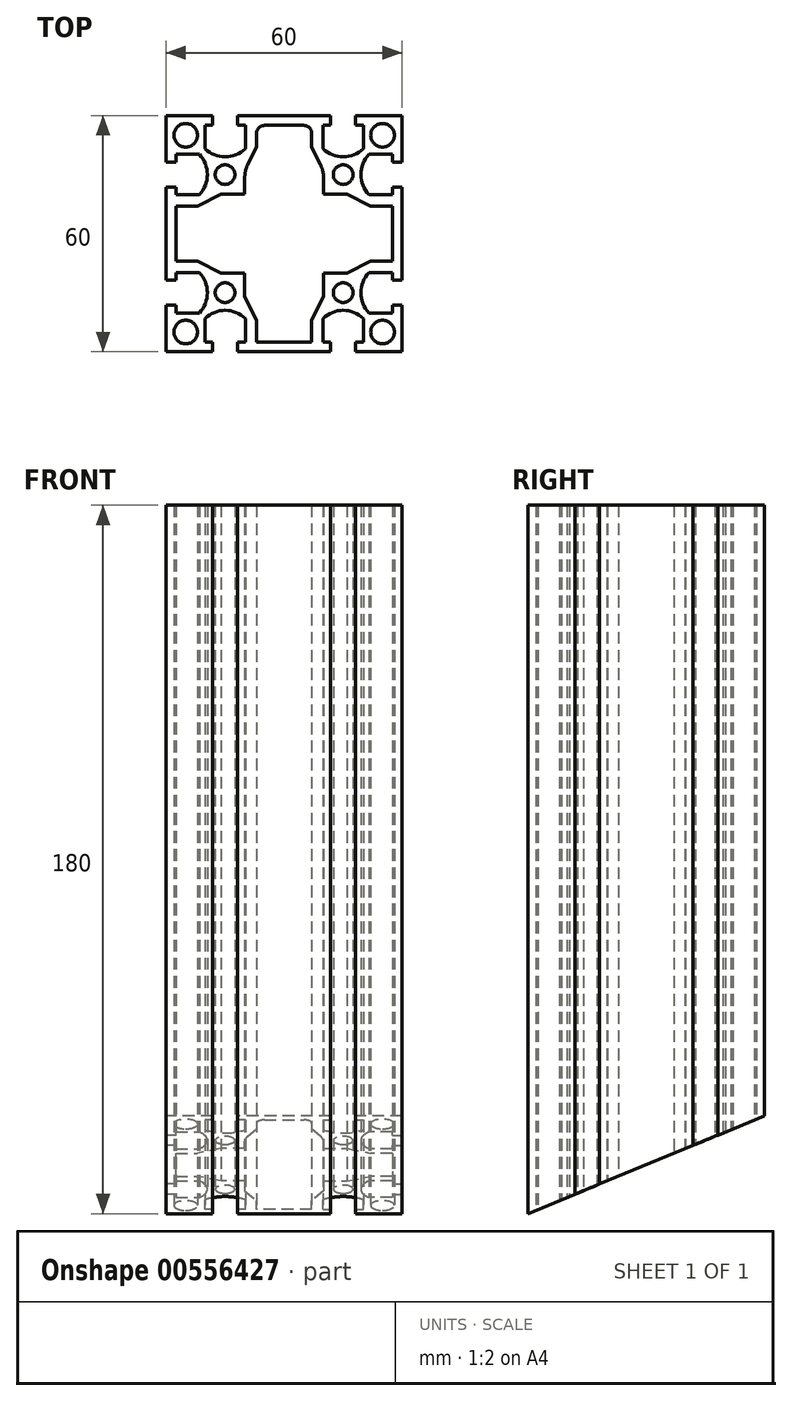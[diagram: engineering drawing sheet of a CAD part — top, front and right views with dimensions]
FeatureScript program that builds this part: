
annotation { "Feature Type Name" : "Feature", "Feature Type Description" : "" }
export const myFeature = defineFeature(function(context is Context, id is Id, definition is map)
    precondition{}
    {
        {
            var Q0;
            Q0=qCreatedBy(makeId("Top.planeOp"),FACE);
            var sketch = newSketch(context, id + "F0", { "sketchPlane" : qUnion([Q0])});
            skLineSegment(sketch, "E0.bottom", {"start": v(30, -30) * mm, "end": v(-30, -30) * mm});
            skLineSegment(sketch, "E0.top", {"start": v(30, 30) * mm, "end": v(-30, 30) * mm});
            skLineSegment(sketch, "E0.left", {"start": v(30, -30) * mm, "end": v(30, 30) * mm});
            skLineSegment(sketch, "E0.right", {"start": v(-30, -30) * mm, "end": v(-30, 30) * mm});
            skPoint(sketch, "E0.middle", {"position": v(0, 0) * mm});
            skLineSegment(sketch, "E1.top", {"start": v(-11.85, 30) * mm, "end": v(-18.15, 30) * mm});
            skLineSegment(sketch, "E1.left", {"start": v(-11.85, 27.5) * mm, "end": v(-11.85, 30) * mm});
            skLineSegment(sketch, "E1.right", {"start": v(-18.15, 27.5) * mm, "end": v(-18.15, 30) * mm});
            skPoint(sketch, "E1.middle", {"position": v(-15, 28.75) * mm});
            skLineSegment(sketch, "E2.bottom", {"start": v(-9.85, 27.5) * mm, "end": v(-11.85, 27.5) * mm});
            skLineSegment(sketch, "E2.left", {"start": v(-9.85, 27.5) * mm, "end": v(-9.85, 21.55) * mm});
            skLineSegment(sketch, "E2.right", {"start": v(-20.15, 27.5) * mm, "end": v(-20.15, 21.55) * mm});
            skPoint(sketch, "E2.middle", {"position": v(-15, 24.52) * mm});
            skArc(sketch, "E3", {"start": v(-20.15, 21.55) * mm, "mid": v(-15, 19.5) * mm, "end": v(-9.85, 21.55) * mm});
            skPoint(sketch, "E4.MirrorP", {"position": v(15, 24.52) * mm});
            skPoint(sketch, "E5.MirrorP", {"position": v(15, 28.75) * mm});
            skLineSegment(sketch, "E6.MirrorCS", {"start": v(11.85, 27.5) * mm, "end": v(11.85, 30) * mm});
            skLineSegment(sketch, "E7.MirrorCS", {"start": v(18.15, 27.5) * mm, "end": v(18.15, 30) * mm});
            skLineSegment(sketch, "E8.MirrorCS", {"start": v(9.85, 27.5) * mm, "end": v(11.85, 27.5) * mm});
            skLineSegment(sketch, "E9.MirrorCS", {"start": v(9.85, 27.5) * mm, "end": v(9.85, 21.55) * mm});
            skArc(sketch, "E10.MirrorCS", {"start": v(20.15, 21.55) * mm, "mid": v(15, 19.5) * mm, "end": v(9.85, 21.55) * mm});
            skLineSegment(sketch, "E11.MirrorCS", {"start": v(20.15, 27.5) * mm, "end": v(20.15, 21.55) * mm});
            skLineSegment(sketch, "E12.MirrorCS", {"start": v(11.85, 30) * mm, "end": v(18.15, 30) * mm});
            skLineSegment(sketch, "E13.1.0", {"start": v(27.5, 20.15) * mm, "end": v(21.55, 20.15) * mm});
            skLineSegment(sketch, "E13.1.1", {"start": v(27.5, 9.85) * mm, "end": v(21.55, 9.85) * mm});
            skArc(sketch, "E13.1.2", {"start": v(21.55, 20.15) * mm, "mid": v(19.5, 15) * mm, "end": v(21.55, 9.85) * mm});
            skLineSegment(sketch, "E13.1.3", {"start": v(27.5, -9.85) * mm, "end": v(21.55, -9.85) * mm});
            skLineSegment(sketch, "E13.1.4", {"start": v(27.5, -20.15) * mm, "end": v(21.55, -20.15) * mm});
            skPoint(sketch, "E13.1.5", {"position": v(28.75, 15) * mm});
            skPoint(sketch, "E13.1.6", {"position": v(28.75, -15) * mm});
            skArc(sketch, "E13.1.7", {"start": v(21.55, -20.15) * mm, "mid": v(19.5, -15) * mm, "end": v(21.55, -9.85) * mm});
            skPoint(sketch, "E13.1.8", {"position": v(24.52, -15) * mm});
            skPoint(sketch, "E13.1.9", {"position": v(24.52, 15) * mm});
            skLineSegment(sketch, "E13.1.10", {"start": v(27.5, 9.85) * mm, "end": v(27.5, 20.15) * mm});
            skLineSegment(sketch, "E13.1.11", {"start": v(27.5, -11.85) * mm, "end": v(27.5, -18.15) * mm});
            skLineSegment(sketch, "E13.1.12", {"start": v(30, 11.85) * mm, "end": v(30, 18.15) * mm});
            skLineSegment(sketch, "E13.1.13", {"start": v(30, -11.85) * mm, "end": v(30, -18.15) * mm});
            skLineSegment(sketch, "E13.1.14", {"start": v(27.5, 18.15) * mm, "end": v(30, 18.15) * mm});
            skLineSegment(sketch, "E13.1.15", {"start": v(27.5, 11.85) * mm, "end": v(30, 11.85) * mm});
            skLineSegment(sketch, "E13.1.16", {"start": v(27.5, 11.85) * mm, "end": v(27.5, 18.15) * mm});
            skLineSegment(sketch, "E13.1.17", {"start": v(27.5, -9.85) * mm, "end": v(27.5, -20.15) * mm});
            skLineSegment(sketch, "E13.1.18", {"start": v(27.5, -18.15) * mm, "end": v(30, -18.15) * mm});
            skLineSegment(sketch, "E13.1.19", {"start": v(27.5, -11.85) * mm, "end": v(30, -11.85) * mm});
            skLineSegment(sketch, "E13.2.0", {"start": v(20.15, -27.5) * mm, "end": v(20.15, -21.55) * mm});
            skLineSegment(sketch, "E13.2.1", {"start": v(9.85, -27.5) * mm, "end": v(9.85, -21.55) * mm});
            skArc(sketch, "E13.2.2", {"start": v(20.15, -21.55) * mm, "mid": v(15, -19.5) * mm, "end": v(9.85, -21.55) * mm});
            skLineSegment(sketch, "E13.2.3", {"start": v(-9.85, -27.5) * mm, "end": v(-9.85, -21.55) * mm});
            skLineSegment(sketch, "E13.2.4", {"start": v(-20.15, -27.5) * mm, "end": v(-20.15, -21.55) * mm});
            skPoint(sketch, "E13.2.5", {"position": v(15, -28.75) * mm});
            skPoint(sketch, "E13.2.6", {"position": v(-15, -28.75) * mm});
            skArc(sketch, "E13.2.7", {"start": v(-20.15, -21.55) * mm, "mid": v(-15, -19.5) * mm, "end": v(-9.85, -21.55) * mm});
            skPoint(sketch, "E13.2.8", {"position": v(-15, -24.52) * mm});
            skPoint(sketch, "E13.2.9", {"position": v(15, -24.52) * mm});
            skLineSegment(sketch, "E13.2.10", {"start": v(9.85, -27.5) * mm, "end": v(20.15, -27.5) * mm});
            skLineSegment(sketch, "E13.2.11", {"start": v(-11.85, -27.5) * mm, "end": v(-18.15, -27.5) * mm});
            skLineSegment(sketch, "E13.2.12", {"start": v(11.85, -30) * mm, "end": v(18.15, -30) * mm});
            skLineSegment(sketch, "E13.2.13", {"start": v(-11.85, -30) * mm, "end": v(-18.15, -30) * mm});
            skLineSegment(sketch, "E13.2.14", {"start": v(18.15, -27.5) * mm, "end": v(18.15, -30) * mm});
            skLineSegment(sketch, "E13.2.15", {"start": v(11.85, -27.5) * mm, "end": v(11.85, -30) * mm});
            skLineSegment(sketch, "E13.2.16", {"start": v(11.85, -27.5) * mm, "end": v(18.15, -27.5) * mm});
            skLineSegment(sketch, "E13.2.17", {"start": v(-9.85, -27.5) * mm, "end": v(-20.15, -27.5) * mm});
            skLineSegment(sketch, "E13.2.18", {"start": v(-18.15, -27.5) * mm, "end": v(-18.15, -30) * mm});
            skLineSegment(sketch, "E13.2.19", {"start": v(-11.85, -27.5) * mm, "end": v(-11.85, -30) * mm});
            skLineSegment(sketch, "E13.3.0", {"start": v(-27.5, -20.15) * mm, "end": v(-21.55, -20.15) * mm});
            skLineSegment(sketch, "E13.3.1", {"start": v(-27.5, -9.85) * mm, "end": v(-21.55, -9.85) * mm});
            skArc(sketch, "E13.3.2", {"start": v(-21.55, -20.15) * mm, "mid": v(-19.5, -15) * mm, "end": v(-21.55, -9.85) * mm});
            skLineSegment(sketch, "E13.3.3", {"start": v(-27.5, 9.85) * mm, "end": v(-21.55, 9.85) * mm});
            skLineSegment(sketch, "E13.3.4", {"start": v(-27.5, 20.15) * mm, "end": v(-21.55, 20.15) * mm});
            skPoint(sketch, "E13.3.5", {"position": v(-28.75, -15) * mm});
            skPoint(sketch, "E13.3.6", {"position": v(-28.75, 15) * mm});
            skArc(sketch, "E13.3.7", {"start": v(-21.55, 20.15) * mm, "mid": v(-19.5, 15) * mm, "end": v(-21.55, 9.85) * mm});
            skPoint(sketch, "E13.3.8", {"position": v(-24.52, 15) * mm});
            skPoint(sketch, "E13.3.9", {"position": v(-24.52, -15) * mm});
            skLineSegment(sketch, "E13.3.10", {"start": v(-27.5, -9.85) * mm, "end": v(-27.5, -20.15) * mm});
            skLineSegment(sketch, "E13.3.11", {"start": v(-27.5, 11.85) * mm, "end": v(-27.5, 18.15) * mm});
            skLineSegment(sketch, "E13.3.12", {"start": v(-30, -11.85) * mm, "end": v(-30, -18.15) * mm});
            skLineSegment(sketch, "E13.3.13", {"start": v(-30, 11.85) * mm, "end": v(-30, 18.15) * mm});
            skLineSegment(sketch, "E13.3.14", {"start": v(-27.5, -18.15) * mm, "end": v(-30, -18.15) * mm});
            skLineSegment(sketch, "E13.3.15", {"start": v(-27.5, -11.85) * mm, "end": v(-30, -11.85) * mm});
            skLineSegment(sketch, "E13.3.16", {"start": v(-27.5, -11.85) * mm, "end": v(-27.5, -18.15) * mm});
            skLineSegment(sketch, "E13.3.17", {"start": v(-27.5, 9.85) * mm, "end": v(-27.5, 20.15) * mm});
            skLineSegment(sketch, "E13.3.18", {"start": v(-27.5, 18.15) * mm, "end": v(-30, 18.15) * mm});
            skLineSegment(sketch, "E13.3.19", {"start": v(-27.5, 11.85) * mm, "end": v(-30, 11.85) * mm});
            skLineSegment(sketch, "E13.anchor1", {"start": v(0, 0) * mm, "end": v(-20.15, 21.55) * mm, "construction": true});
            skLineSegment(sketch, "E13.anchor2", {"start": v(0, 0) * mm, "end": v(-21.55, -20.15) * mm, "construction": true});
            skLineSegment(sketch, "E14.trimOffspring", {"start": v(-18.15, 27.5) * mm, "end": v(-20.15, 27.5) * mm});
            skLineSegment(sketch, "E15.trimOffspring", {"start": v(18.15, 27.5) * mm, "end": v(20.15, 27.5) * mm});
            skCircle(sketch, "E16", {"center": v(-15, 15) * mm, "radius": 2.5 * mm});
            skCircle(sketch, "E17", {"center": v(-25, 25) * mm, "radius": 3 * mm});
            skCircle(sketch, "E18.MirrorC", {"center": v(25, 25) * mm, "radius": 3 * mm});
            skCircle(sketch, "E19.MirrorC", {"center": v(25, -25) * mm, "radius": 3 * mm});
            skCircle(sketch, "E20.MirrorC", {"center": v(-25, -25) * mm, "radius": 3 * mm});
            skCircle(sketch, "E21.MirrorC", {"center": v(15, 15) * mm, "radius": 2.5 * mm});
            skCircle(sketch, "E22.MirrorC", {"center": v(15, -15) * mm, "radius": 2.5 * mm});
            skCircle(sketch, "E23.MirrorC", {"center": v(-15, -15) * mm, "radius": 2.5 * mm});
            skLineSegment(sketch, "E24", {"start": v(-7, 27.5) * mm, "end": v(0, 27.5) * mm});
            skLineSegment(sketch, "E25", {"start": v(-7, 27.5) * mm, "end": v(-7, 22) * mm});
            skLineSegment(sketch, "E26", {"start": v(-10, 10) * mm, "end": v(-10, 16) * mm});
            skLineSegment(sketch, "E27", {"start": v(-10, 16) * mm, "end": v(-7, 22) * mm});
            skLineSegment(sketch, "E28.MirrorCS", {"start": v(10, 10) * mm, "end": v(10, 16) * mm});
            skLineSegment(sketch, "E29.MirrorCS", {"start": v(10, 16) * mm, "end": v(7, 22) * mm});
            skLineSegment(sketch, "E30.MirrorCS", {"start": v(7, 27.5) * mm, "end": v(0, 27.5) * mm});
            skLineSegment(sketch, "E31.MirrorCS", {"start": v(7, 27.5) * mm, "end": v(7, 22) * mm});
            skLineSegment(sketch, "E32.1.0", {"start": v(-10, -10) * mm, "end": v(-16, -10) * mm});
            skLineSegment(sketch, "E32.1.1", {"start": v(-16, -10) * mm, "end": v(-22, -7) * mm});
            skLineSegment(sketch, "E32.1.2", {"start": v(-27.5, -7) * mm, "end": v(-22, -7) * mm});
            skLineSegment(sketch, "E32.1.3", {"start": v(-27.5, -7) * mm, "end": v(-27.5, 0) * mm});
            skLineSegment(sketch, "E32.1.4", {"start": v(-27.5, 7) * mm, "end": v(-27.5, 0) * mm});
            skLineSegment(sketch, "E32.1.5", {"start": v(-27.5, 7) * mm, "end": v(-22, 7) * mm});
            skLineSegment(sketch, "E32.1.6", {"start": v(-16, 10) * mm, "end": v(-22, 7) * mm});
            skLineSegment(sketch, "E32.1.7", {"start": v(-10, 10) * mm, "end": v(-16, 10) * mm});
            skLineSegment(sketch, "E32.2.0", {"start": v(10, -10) * mm, "end": v(10, -16) * mm});
            skLineSegment(sketch, "E32.2.1", {"start": v(10, -16) * mm, "end": v(7, -22) * mm});
            skLineSegment(sketch, "E32.2.2", {"start": v(7, -27.5) * mm, "end": v(7, -22) * mm});
            skLineSegment(sketch, "E32.2.3", {"start": v(7, -27.5) * mm, "end": v(0, -27.5) * mm});
            skLineSegment(sketch, "E32.2.4", {"start": v(-7, -27.5) * mm, "end": v(0, -27.5) * mm});
            skLineSegment(sketch, "E32.2.5", {"start": v(-7, -27.5) * mm, "end": v(-7, -22) * mm});
            skLineSegment(sketch, "E32.2.6", {"start": v(-10, -16) * mm, "end": v(-7, -22) * mm});
            skLineSegment(sketch, "E32.2.7", {"start": v(-10, -10) * mm, "end": v(-10, -16) * mm});
            skLineSegment(sketch, "E32.3.0", {"start": v(10, 10) * mm, "end": v(16, 10) * mm});
            skLineSegment(sketch, "E32.3.1", {"start": v(16, 10) * mm, "end": v(22, 7) * mm});
            skLineSegment(sketch, "E32.3.2", {"start": v(27.5, 7) * mm, "end": v(22, 7) * mm});
            skLineSegment(sketch, "E32.3.3", {"start": v(27.5, 7) * mm, "end": v(27.5, 0) * mm});
            skLineSegment(sketch, "E32.3.4", {"start": v(27.5, -7) * mm, "end": v(27.5, 0) * mm});
            skLineSegment(sketch, "E32.3.5", {"start": v(27.5, -7) * mm, "end": v(22, -7) * mm});
            skLineSegment(sketch, "E32.3.6", {"start": v(16, -10) * mm, "end": v(22, -7) * mm});
            skLineSegment(sketch, "E32.3.7", {"start": v(10, -10) * mm, "end": v(16, -10) * mm});
            skSolve(sketch);
        }
        {
            var Q0;
            {var subQ30=sQuery(id+"F0.wireOp",EDGE,"E1.left");Q0=makeQuery(id+"F0.imprint","IMPRINT",FACE,{"disambiguationData":[TD([[makeQuery(id+"F0.imprint","IMPRINT",EDGE,{"derivedFrom":subQ30}),-1.0]])]});}
            extrude(context, id + "F1", {"entities" : qUnion([Q0]), "depth" : 180 * mm, "offsetDistance" : 25 * mm});
        }
        {
            var Q0;
            Q0=makeQuery(id+"F1.opExtrude","SWEPT_EDGE",EDGE,{"disambiguationData":[OSD([sQuery(id+"F0.wireOp",EDGE,"E24"),sQuery(id+"F0.wireOp",EDGE,"E25")])]});
            var Q1;
            Q1=makeQuery(id+"F1.opExtrude","SWEPT_EDGE",EDGE,{"disambiguationData":[OSD([sQuery(id+"F0.wireOp",EDGE,"E30.MirrorCS"),sQuery(id+"F0.wireOp",EDGE,"E31.MirrorCS")])]});
            var Q2;
            Q2=makeQuery(id+"F1.opExtrude","SWEPT_EDGE",EDGE,{"disambiguationData":[OSD([sQuery(id+"F0.wireOp",EDGE,"840db5bc-c403-45cd-90c7-254e62d9e8c5.3.2"),sQuery(id+"F0.wireOp",EDGE,"840db5bc-c403-45cd-90c7-254e62d9e8c5.3.3")])]});
            var Q3;
            Q3=makeQuery(id+"F1.opExtrude","SWEPT_EDGE",EDGE,{"disambiguationData":[OSD([sQuery(id+"F0.wireOp",EDGE,"840db5bc-c403-45cd-90c7-254e62d9e8c5.3.4"),sQuery(id+"F0.wireOp",EDGE,"840db5bc-c403-45cd-90c7-254e62d9e8c5.3.5")])]});
            var Q4;
            Q4=makeQuery(id+"F1.opExtrude","SWEPT_EDGE",EDGE,{"disambiguationData":[OSD([sQuery(id+"F0.wireOp",EDGE,"840db5bc-c403-45cd-90c7-254e62d9e8c5.1.4"),sQuery(id+"F0.wireOp",EDGE,"840db5bc-c403-45cd-90c7-254e62d9e8c5.1.5")])]});
            var Q5;
            Q5=makeQuery(id+"F1.opExtrude","SWEPT_EDGE",EDGE,{"disambiguationData":[OSD([sQuery(id+"F0.wireOp",EDGE,"840db5bc-c403-45cd-90c7-254e62d9e8c5.1.2"),sQuery(id+"F0.wireOp",EDGE,"840db5bc-c403-45cd-90c7-254e62d9e8c5.1.3")])]});
            var Q6;
            Q6=makeQuery(id+"F1.opExtrude","SWEPT_EDGE",EDGE,{"disambiguationData":[OSD([sQuery(id+"F0.wireOp",EDGE,"840db5bc-c403-45cd-90c7-254e62d9e8c5.2.2"),sQuery(id+"F0.wireOp",EDGE,"840db5bc-c403-45cd-90c7-254e62d9e8c5.2.3")])]});
            var Q7;
            Q7=makeQuery(id+"F1.opExtrude","SWEPT_EDGE",EDGE,{"disambiguationData":[OSD([sQuery(id+"F0.wireOp",EDGE,"840db5bc-c403-45cd-90c7-254e62d9e8c5.2.4"),sQuery(id+"F0.wireOp",EDGE,"840db5bc-c403-45cd-90c7-254e62d9e8c5.2.5")])]});
            fillet(context, id + "F2", {"entities" : qUnion([Q0, Q1, Q2, Q3, Q4, Q5, Q6, Q7]), "radius" : 2 * mm, "tangentPropagation" : true, "allowEdgeOverflow" : false});
        }
        {
            var Q0;
            Q0=makeQuery(id+"F1.opExtrude","SWEPT_EDGE",EDGE,{"disambiguationData":[OSD([sQuery(id+"F0.wireOp",EDGE,"E26"),sQuery(id+"F0.wireOp",EDGE,"E27")])]});
            var Q1;
            Q1=makeQuery(id+"F1.opExtrude","SWEPT_EDGE",EDGE,{"disambiguationData":[OSD([sQuery(id+"F0.wireOp",EDGE,"E28.MirrorCS"),sQuery(id+"F0.wireOp",EDGE,"E29.MirrorCS")])]});
            var Q2;
            Q2=makeQuery(id+"F1.opExtrude","SWEPT_EDGE",EDGE,{"disambiguationData":[OSD([sQuery(id+"F0.wireOp",EDGE,"840db5bc-c403-45cd-90c7-254e62d9e8c5.3.0"),sQuery(id+"F0.wireOp",EDGE,"840db5bc-c403-45cd-90c7-254e62d9e8c5.3.1")])]});
            var Q3;
            Q3=makeQuery(id+"F1.opExtrude","SWEPT_EDGE",EDGE,{"disambiguationData":[OSD([sQuery(id+"F0.wireOp",EDGE,"840db5bc-c403-45cd-90c7-254e62d9e8c5.1.6"),sQuery(id+"F0.wireOp",EDGE,"840db5bc-c403-45cd-90c7-254e62d9e8c5.1.7")])]});
            var Q4;
            Q4=makeQuery(id+"F1.opExtrude","SWEPT_EDGE",EDGE,{"disambiguationData":[OSD([sQuery(id+"F0.wireOp",EDGE,"840db5bc-c403-45cd-90c7-254e62d9e8c5.1.0"),sQuery(id+"F0.wireOp",EDGE,"840db5bc-c403-45cd-90c7-254e62d9e8c5.1.1")])]});
            var Q5;
            Q5=makeQuery(id+"F1.opExtrude","SWEPT_EDGE",EDGE,{"disambiguationData":[OSD([sQuery(id+"F0.wireOp",EDGE,"840db5bc-c403-45cd-90c7-254e62d9e8c5.3.6"),sQuery(id+"F0.wireOp",EDGE,"840db5bc-c403-45cd-90c7-254e62d9e8c5.3.7")])]});
            var Q6;
            Q6=makeQuery(id+"F1.opExtrude","SWEPT_EDGE",EDGE,{"disambiguationData":[OSD([sQuery(id+"F0.wireOp",EDGE,"840db5bc-c403-45cd-90c7-254e62d9e8c5.2.0"),sQuery(id+"F0.wireOp",EDGE,"840db5bc-c403-45cd-90c7-254e62d9e8c5.2.1")])]});
            var Q7;
            Q7=makeQuery(id+"F1.opExtrude","SWEPT_EDGE",EDGE,{"disambiguationData":[OSD([sQuery(id+"F0.wireOp",EDGE,"840db5bc-c403-45cd-90c7-254e62d9e8c5.2.6"),sQuery(id+"F0.wireOp",EDGE,"840db5bc-c403-45cd-90c7-254e62d9e8c5.2.7")])]});
            fillet(context, id + "F3", {"entities" : qUnion([Q0, Q1, Q2, Q3, Q4, Q5, Q6, Q7]), "radius" : 7 * mm, "tangentPropagation" : true, "allowEdgeOverflow" : false});
        }
        {
            var Q0;
            {var subQ0=sQuery(id+"F0.wireOp",EDGE,"E0.bottom");Q0=makeQuery(id+"F1.opExtrude","SWEPT_FACE",FACE,{"disambiguationData":[OSD([subQ0]),TDD([makeQuery(id+"F0.imprint","IMPRINT",EDGE,{"disambiguationData":[TD([[makeQuery(id+"F0.imprint","INTERSECT",VERTEX,{"derivedFrom":[subQ0,sQuery(id+"F0.wireOp",EDGE,"E13.2.12"),sQuery(id+"F0.wireOp",EDGE,"E13.2.15")]}),-1.0]])],"derivedFrom":subQ0})])]});}
            var sketch = newSketch(context, id + "F4", { "sketchPlane" : qUnion([Q0])});
            skLineSegment(sketch, "E33.0", {"start": v(-18.15, 180) * mm, "end": v(-30, 180) * mm});
            skLineSegment(sketch, "E33.1", {"start": v(30, 180) * mm, "end": v(30, 0) * mm});
            skLineSegment(sketch, "E34", {"start": v(-30, 180) * mm, "end": v(30, 180) * mm});
            skLineSegment(sketch, "E35", {"start": v(30, 120) * mm, "end": v(-30, 180) * mm});
            skLineSegment(sketch, "E36.0", {"start": v(-18.15, 0) * mm, "end": v(-30, 0) * mm});
            skLineSegment(sketch, "E37", {"start": v(-30, 0) * mm, "end": v(30, 0) * mm});
            skLineSegment(sketch, "E38", {"start": v(30, 60) * mm, "end": v(-30, 0) * mm});
            skSolve(sketch);
        }
        {
            var Q0;
            Q0=qCreatedBy(makeId("Right.planeOp"),FACE);
            var sketch = newSketch(context, id + "F5", { "sketchPlane" : qUnion([Q0])});
            skLineSegment(sketch, "E39.bottom", {"start": v(145.98, 72.9) * mm, "end": v(-30, 0) * mm});
            skLineSegment(sketch, "E39.top", {"start": v(189.02, -31) * mm, "end": v(13.04, -103.9) * mm});
            skLineSegment(sketch, "E39.left", {"start": v(145.98, 72.9) * mm, "end": v(189.02, -31) * mm});
            skLineSegment(sketch, "E39.right", {"start": v(-30, 0) * mm, "end": v(13.04, -103.9) * mm});
            skSolve(sketch);
        }
        {
            var Q0;
            Q0=qSketchRegion(id+"F5",true);
            extrude(context, id + "F6", {"entities" : qUnion([Q0]), "operationType" : NewBodyOperationType.REMOVE, "oppositeDirection" : true, "depth" : 30 * mm, "offsetDistance" : 25 * mm, "hasSecondDirection" : true, "secondDirectionOppositeDirection" : false, "secondDirectionDepth" : 30 * mm});
        }
    });
